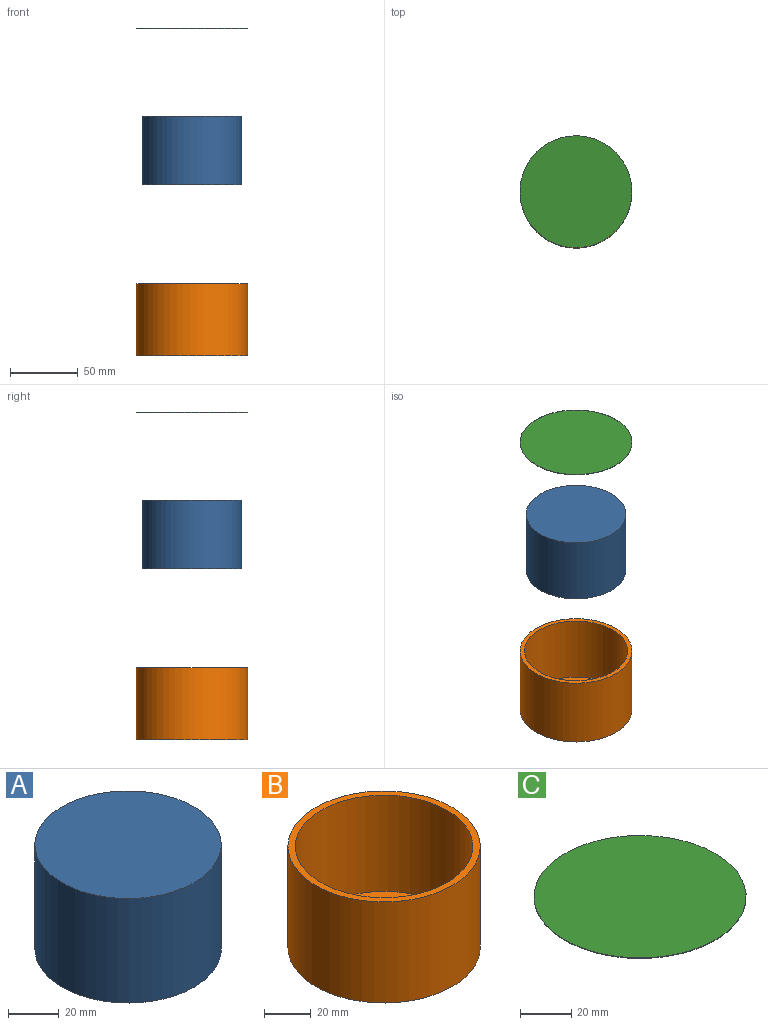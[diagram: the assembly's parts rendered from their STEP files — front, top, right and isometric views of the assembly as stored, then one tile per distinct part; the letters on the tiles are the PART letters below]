
ASSEMBLY  parts=3 mates=2
PART A: 3 faces, bbox 73.7x73.7x50.5 mm
  f0: cylinder r=36.83mm len=73.66mm, axis (0,0,-1), area 11696.8mm2, adj f1,f2
  f1: plane 73.66x73.66mm, normal (0,0,1), area 4261.4mm2, adj f0
  f2: plane 73.66x73.66mm, normal (0,0,-1), area 4261.4mm2, adj f0
PART B: 5 faces, bbox 82.6x82.6x53.1 mm
  f0: cylinder r=38.1mm len=76.2mm, axis (0,0,-1), area 12100.2mm2, adj f2,f3
  f1: cylinder r=41.27mm len=82.55mm, axis (0,0,-1), area 13767.2mm2, adj f2,f4
  f2: plane 82.55x82.55mm, normal (0,0,1), area 791.7mm2, adj f0,f1
  f3: plane 76.2x76.2mm, normal (0,0,1), area 4560.4mm2, adj f0
  f4: plane 82.55x82.55mm, normal (0,0,-1), area 5352.1mm2, adj f1
PART C: 3 faces, bbox 82.6x82.6x0.3 mm
  f0: cylinder r=41.27mm len=82.55mm, axis (0,0,-1), area 65.9mm2, adj f1,f2
  f1: plane 82.55x82.55mm, normal (0,0,1), area 5352.1mm2, adj f0
  f2: plane 82.55x82.55mm, normal (0,0,-1), area 5352.1mm2, adj f0
PLACE A t=(-78.87,-89.88,6.88)mm
PLACE B t=(-78.87,-89.88,-116.75)mm
PLACE C t=(-78.87,-89.88,122.08)mm
MATE cylindrical A.f0 <-> B.f0  axis (0,0,-1) through (-78.87,-89.88,32.15)mm
MATE cylindrical A.f0 <-> C.f0  axis (0,0,1) through (-78.87,-89.88,57.42)mm
